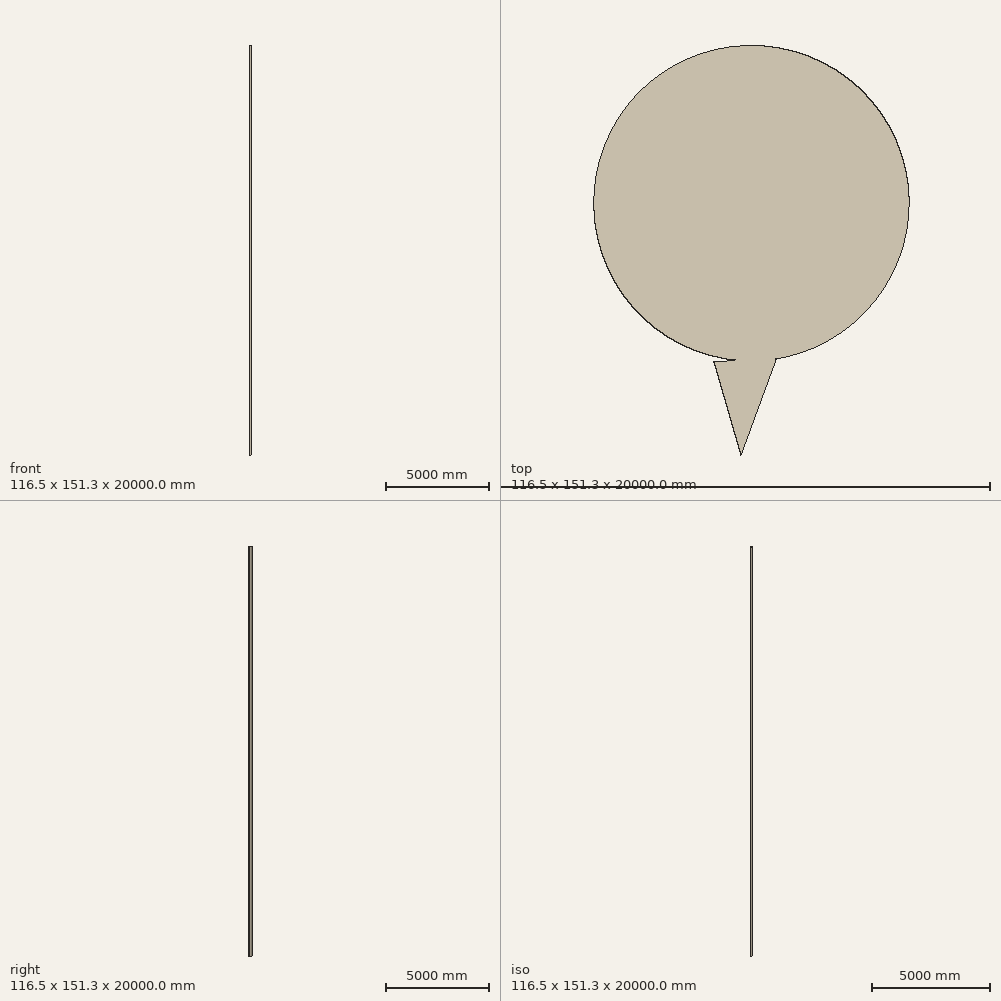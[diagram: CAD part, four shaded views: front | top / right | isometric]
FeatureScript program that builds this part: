
annotation { "Feature Type Name" : "Feature", "Feature Type Description" : "" }
export const myFeature = defineFeature(function(context is Context, id is Id, definition is map)
    precondition{}
    {
        {
            var Q0;
            Q0=qCreatedBy(makeId("Top.planeOp"),FACE);
            var sketch = newSketch(context, id + "F0", { "sketchPlane" : qUnion([Q0])});
            skLineSegment(sketch, "E0", {"start": v(-10.07, -40.74) * mm, "end": v(0, -75.48) * mm});
            skLineSegment(sketch, "E1", {"start": v(0, -75.48) * mm, "end": v(13, -40.15) * mm});
            skLineSegment(sketch, "E2", {"start": v(13, -40.15) * mm, "end": v(-10.07, -40.74) * mm});
            skCircle(sketch, "E3", {"center": v(3.83, 17.63) * mm, "radius": 58.23 * mm});
            skPoint(sketch, "E3.first.point", {"position": v(0, -40.48) * mm});
            skPoint(sketch, "E3.second.point", {"position": v(-2.77, 75.48) * mm});
            skPoint(sketch, "E3.third.point", {"position": v(-54.17, 12.41) * mm});
            skSolve(sketch);
        }
        {
            var Q0;
            {var subQ1=sQuery(id+"F0.wireOp",EDGE,"E0");Q0=makeQuery(id+"F0.imprint","IMPRINT",FACE,{"disambiguationData":[TD([[makeQuery(id+"F0.imprint","IMPRINT",EDGE,{"derivedFrom":subQ1}),1.0]])]});}
            var Q1;
            {var subQ0=sQuery(id+"F0.wireOp",EDGE,"E3");var subQ1=sQuery(id+"F0.wireOp",EDGE,"E2");var subQ2=makeQuery(id+"F0.imprint","INTERSECT",VERTEX,{"disambiguationData":[OD(0.0)],"derivedFrom":[subQ1,subQ0]});Q1=makeQuery(id+"F0.imprint","IMPRINT",FACE,{"disambiguationData":[TD([[makeQuery(id+"F0.imprint","IMPRINT",EDGE,{"disambiguationData":[TD([[subQ2,-1.0]])],"derivedFrom":subQ1}),1.0]])]});}
            extrude(context, id + "F1", {"entities" : qUnion([Q0, Q1]), "depth" : 5 * mm, "offsetDistance" : 25 * mm});
        }
        {
            var Q0;
            Q0 = qSketchRegion(id + "F0", true);
            extrude(context, id + "F2", {"entities" : qUnion([Q0]), "operationType" : NewBodyOperationType.ADD, "depth" : 20000 * mm, "offsetDistance" : 25 * mm});
        }
    });
